# Revit family: Basin-Caroma Integra 500 Wall Vanity
name_source: partatom
category: Plumbing Fixtures
revit_build: Autodesk Revit MEP 2012 (Build: 20110309_2315(x64)
units: mm (PartAtom-declared; Revit-internal decimal feet)

## types (3) — shared parameters
CW Connection = No
Default Elevation = 690 mm
Description = Integra 500 Wall Basin
HW Connection = No
Manufacturer = Caroma
PlumbingMaterial_ANZRS = Porcelain-White-Caroma
Type Comments = Vitreous China Wall Basin
URL = www.caroma.com.au
Vent Connection = No
Waste = Metal-Chrome-Caroma
Waste Connection = Yes

## per-type parameters (varying)
| type | 1 Taphole | 3 Tapholes | Model | Spout Penetration | Tap Penetrations |
| Integra - 3 Tap Holes | No | Yes | 648230 | 0 mm  [stored 0 ft] | 0 mm  [stored 0 ft] |
| Integra - 1 Tap Hole | Yes | No | 648210 | 0 mm  [stored 0 ft] | 100 mm  [stored 0.328084 ft] |
| Integra - 0 Tap Holes | No | No | 648200 | 100 mm  [stored 0.328084 ft] | 100 mm  [stored 0.328084 ft] |

note: [stored X ft] marks values corroborated as IEEE doubles in the binary element streams (Revit-internal decimal feet)

## geometry (parser evidence)
native form markers: Sweep x2
no freeform markers — native parametric forms only
